# Revit family: Haworth_BelongPlus_Screen_HAB Limited
name_source: partatom
category: Furniture Systems
revit_build: Autodesk Revit 2018 (Build: 20170223_1515(x64)
units: mm (PartAtom-declared; Revit-internal decimal feet)

## family parameters
Always vertical = Yes
Cut with Voids When Loaded = No
OmniClass Number = 23.40.70.14.64.21
OmniClass Title = Systems Furniture
Part Type = Normal
Room Calculation Point = No
Round Connector Dimension = Use Diameter
Shared = No
Work Plane-Based = No

## types (1)
- Back or End Screen - 25h 58w
    Actual Height = 25"
    Actual Mounting Height = 27 13/16"
    Actual Width = 57 1/2"
    Assembly Code = E2020200
    Bracket Finish = Haworth _ Metal _ Brushed Aluminum
    Bracket Offset = 4 3/8"
    Bracket Spacing = 47 1/2"
    Bracket Width = 1 1/4"
    Description = Haworth - Belong Plus - Screen
    Height = 25"
    Manufacturer = Haworth
    Max. Height = 25"
    Max. Width = 58"
    Middle Bracket = Yes
    Min. Height = 17"
    Min. Width = 24"
    Model = Haworth - Belong Plus - Screen
    Panel Bottom Offset = 0"
    Revision Number = 1
    Screen Depth = 7/8"
    Screen Finish = Haworth _ Fabric _ Tellure _ Miami 3A-33
    Size = Verify Final Dim. w/ Haworth
    Standard Heights = 17in. or 25 in.
    Standard Widths = 23-58 in.
    Sustainability Info = https://www.haworth.com
    URL = http://www.haworth.com
    URL - Product = http://www.haworth.com
    Warranty = http://www.haworth.com
    Width = 58"
    Worksurface Height = 29"
    Worksurface Thickness = 1 3/16"

## geometry (parser evidence)
native form markers: Sweep x3
no freeform markers — native parametric forms only
